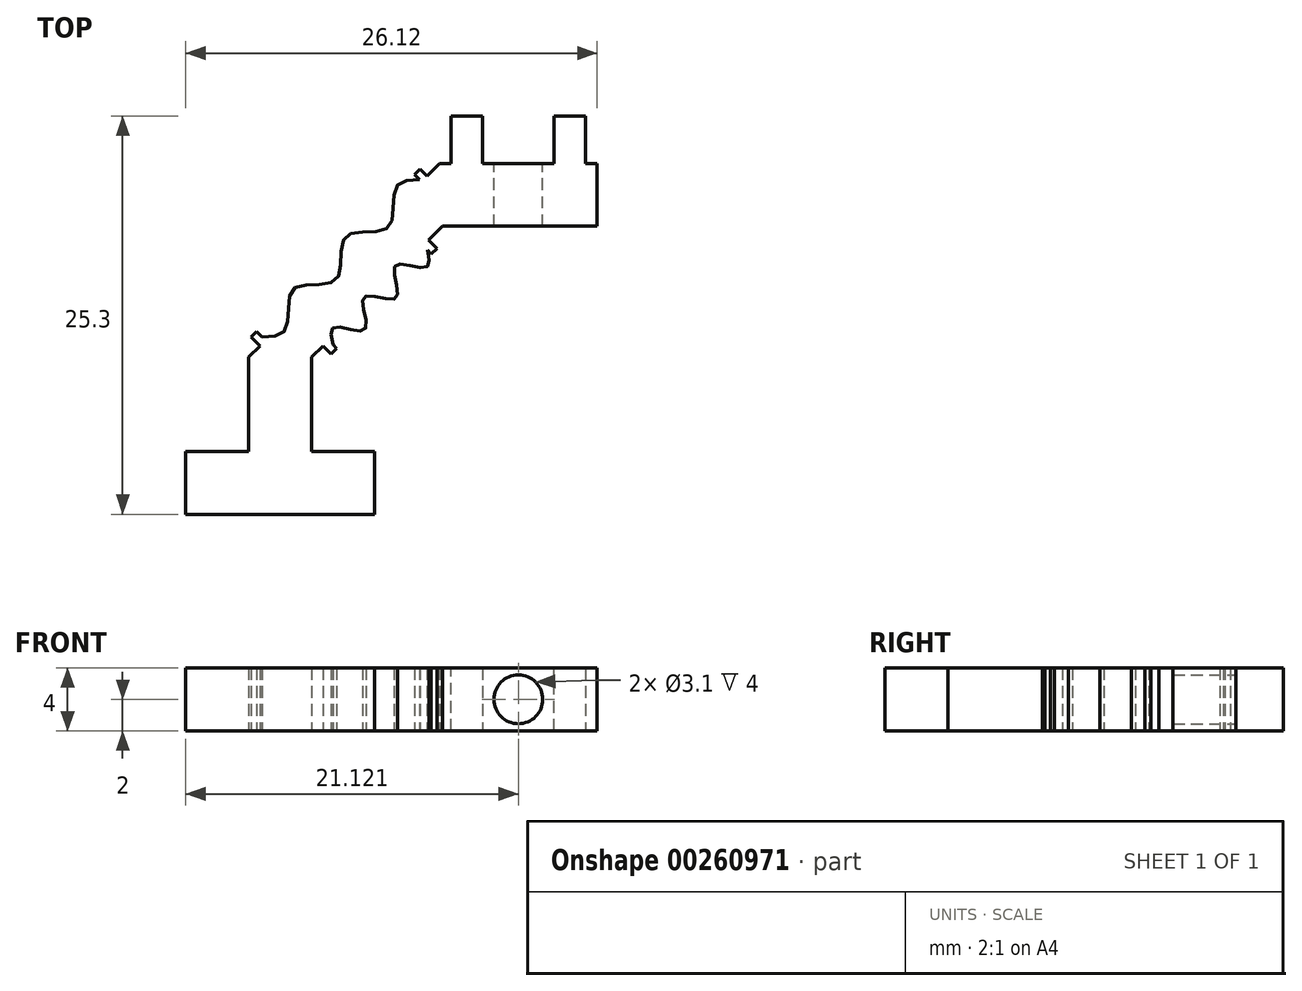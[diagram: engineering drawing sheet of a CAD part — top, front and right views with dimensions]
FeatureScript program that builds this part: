
annotation { "Feature Type Name" : "Feature", "Feature Type Description" : "" }
export const myFeature = defineFeature(function(context is Context, id is Id, definition is map)
    precondition{}
    {
        {
            var Q0;
            Q0=qCreatedBy(makeId("Top.planeOp"),FACE);
            var sketch = newSketch(context, id + "F0", { "sketchPlane" : qUnion([Q0])});
            skLineSegment(sketch, "E0", {"start": v(8, 0) * mm, "end": v(4, 0) * mm});
            skLineSegment(sketch, "E1", {"start": v(4, 4) * mm, "end": v(4, 10) * mm});
            skLineSegment(sketch, "E2", {"start": v(8, 4) * mm, "end": v(12, 4) * mm});
            skLineSegment(sketch, "E3", {"start": v(12, 4) * mm, "end": v(12, 0) * mm});
            skLineSegment(sketch, "E4", {"start": v(12, 0) * mm, "end": v(8, 0) * mm});
            skLineSegment(sketch, "E5", {"start": v(4, 0) * mm, "end": v(0, 0) * mm});
            skLineSegment(sketch, "E6", {"start": v(0, 0) * mm, "end": v(0, 4) * mm});
            skLineSegment(sketch, "E7", {"start": v(0, 4) * mm, "end": v(4, 4) * mm});
            skLineSegment(sketch, "E8", {"start": v(8, 4) * mm, "end": v(8, 10) * mm});
            skLineSegment(sketch, "E9", {"start": v(5.33, 10.8) * mm, "end": v(7, 12.46) * mm, "construction": true});
            skLineSegment(sketch, "E10", {"start": v(7, 12.46) * mm, "end": v(8.66, 14.13) * mm, "construction": true});
            skLineSegment(sketch, "E11", {"start": v(8.66, 14.13) * mm, "end": v(10.33, 15.8) * mm, "construction": true});
            skLineSegment(sketch, "E12", {"start": v(10.33, 15.8) * mm, "end": v(12, 17.46) * mm, "construction": true});
            skLineSegment(sketch, "E13", {"start": v(12, 17.46) * mm, "end": v(13.66, 19.13) * mm, "construction": true});
            skLineSegment(sketch, "E14", {"start": v(13.66, 19.13) * mm, "end": v(15.33, 20.8) * mm, "construction": true});
            skLineSegment(sketch, "E15", {"start": v(6.16, 11.63) * mm, "end": v(6.69, 11.1) * mm, "construction": true});
            skLineSegment(sketch, "E16", {"start": v(7.83, 13.3) * mm, "end": v(7.3, 13.83) * mm, "construction": true});
            skLineSegment(sketch, "E17", {"start": v(9.5, 14.96) * mm, "end": v(10.02, 14.43) * mm, "construction": true});
            skLineSegment(sketch, "E18", {"start": v(11.16, 16.63) * mm, "end": v(10.63, 17.16) * mm, "construction": true});
            skLineSegment(sketch, "E19", {"start": v(12.83, 18.3) * mm, "end": v(13.36, 17.77) * mm, "construction": true});
            skLineSegment(sketch, "E20", {"start": v(14.5, 19.96) * mm, "end": v(13.96, 20.5) * mm, "construction": true});
            skLineSegment(sketch, "E21", {"start": v(8.8, 11.33) * mm, "end": v(9.8, 12.33) * mm, "construction": true});
            skLineSegment(sketch, "E22", {"start": v(9.8, 12.33) * mm, "end": v(10.8, 13.33) * mm, "construction": true});
            skLineSegment(sketch, "E23", {"start": v(10.8, 13.33) * mm, "end": v(11.8, 14.33) * mm, "construction": true});
            skLineSegment(sketch, "E24", {"start": v(11.8, 14.33) * mm, "end": v(12.8, 15.33) * mm, "construction": true});
            skLineSegment(sketch, "E25", {"start": v(12.8, 15.33) * mm, "end": v(13.8, 16.33) * mm, "construction": true});
            skLineSegment(sketch, "E26", {"start": v(13.8, 16.33) * mm, "end": v(14.8, 17.33) * mm, "construction": true});
            skLineSegment(sketch, "E27", {"start": v(9.3, 11.83) * mm, "end": v(8.77, 12.36) * mm, "construction": true});
            skLineSegment(sketch, "E28", {"start": v(10.3, 12.83) * mm, "end": v(10.83, 12.3) * mm});
            skLineSegment(sketch, "E29", {"start": v(11.3, 13.83) * mm, "end": v(10.77, 14.36) * mm, "construction": true});
            skLineSegment(sketch, "E30", {"start": v(12.3, 14.83) * mm, "end": v(12.83, 14.3) * mm, "construction": true});
            skLineSegment(sketch, "E31", {"start": v(13.3, 15.83) * mm, "end": v(12.77, 16.36) * mm, "construction": true});
            skLineSegment(sketch, "E32", {"start": v(14.3, 16.83) * mm, "end": v(14.83, 16.3) * mm, "construction": true});
            skFitSpline(sketch, "E33", {"points": [v(5.27, 10.85) * mm, v(6.64, 11.15) * mm, v(6.94, 12.52) * mm, v(7.24, 13.88) * mm, v(8.6, 14.18) * mm, v(9.97, 14.48) * mm, v(10.27, 15.85) * mm, v(10.58, 17.21) * mm, v(11.94, 17.52) * mm, v(13.3, 17.82) * mm, v(13.6, 19.18) * mm, v(13.9, 20.55) * mm, v(15.27, 20.85) * mm], "startDerivative": vector(19.55, 0.45) * mm, "endDerivative": vector(19.55, 0.45) * mm});
            skLineSegment(sketch, "E34", {"start": v(15.33, 20.8) * mm, "end": v(14.8, 21.33) * mm});
            skFitSpline(sketch, "E35", {"points": [v(8.78, 11.34) * mm, v(8.75, 12.37) * mm, v(9.78, 12.34) * mm, v(10.8, 12.31) * mm, v(10.78, 13.34) * mm, v(10.75, 14.37) * mm, v(11.78, 14.34) * mm, v(12.8, 14.31) * mm, v(12.78, 15.34) * mm, v(12.75, 16.37) * mm, v(13.78, 16.34) * mm, v(14.8, 16.31) * mm, v(14.78, 17.34) * mm], "startDerivative": vector(-3.55, 15.55) * mm, "endDerivative": vector(-3.54, 15.55) * mm});
            skFitSpline(sketch, "E36", {"points": [v(9.34, 10.78) * mm, v(9.31, 11.8) * mm, v(10.34, 11.78) * mm, v(11.37, 11.75) * mm, v(11.34, 12.78) * mm, v(11.31, 13.8) * mm, v(12.34, 13.78) * mm, v(13.37, 13.75) * mm, v(13.34, 14.78) * mm, v(13.31, 15.8) * mm, v(14.34, 15.78) * mm, v(15.37, 15.75) * mm, v(15.34, 16.78) * mm], "startDerivative": vector(-3.55, 15.55) * mm, "endDerivative": vector(-3.54, 15.55) * mm});
            skLineSegment(sketch, "E37", {"start": v(16.3, 18.3) * mm, "end": v(26.12, 18.3) * mm});
            skLineSegment(sketch, "E38", {"start": v(26.12, 18.3) * mm, "end": v(26.12, 22.3) * mm});
            skLineSegment(sketch, "E39", {"start": v(26.12, 22.3) * mm, "end": v(16.12, 22.3) * mm});
            skLineSegment(sketch, "E40", {"start": v(8, 10) * mm, "end": v(8.88, 10.88) * mm});
            skLineSegment(sketch, "E41", {"start": v(14.53, 17.6) * mm, "end": v(14.88, 17.94) * mm});
            skLineSegment(sketch, "E42", {"start": v(15.6, 16.53) * mm, "end": v(15.94, 16.88) * mm});
            skLineSegment(sketch, "E43", {"start": v(15.94, 16.88) * mm, "end": v(14.88, 17.94) * mm});
            skLineSegment(sketch, "E44", {"start": v(15.41, 17.41) * mm, "end": v(16.3, 18.3) * mm});
            skPoint(sketch, "E45.endSnap0", {"position": v(5.46, 10.66) * mm});
            skLineSegment(sketch, "E46", {"start": v(4, 10) * mm, "end": v(4.88, 10.88) * mm});
            skLineSegment(sketch, "E47", {"start": v(15.33, 20.8) * mm, "end": v(15.41, 20.7) * mm});
            skLineSegment(sketch, "E48", {"start": v(14.8, 21.33) * mm, "end": v(14.53, 21.6) * mm});
            skLineSegment(sketch, "E49", {"start": v(14.53, 21.6) * mm, "end": v(14.88, 21.94) * mm});
            skLineSegment(sketch, "E50", {"start": v(15.41, 20.7) * mm, "end": v(15.77, 21.06) * mm});
            skLineSegment(sketch, "E51", {"start": v(14.88, 21.94) * mm, "end": v(15.77, 21.06) * mm});
            skLineSegment(sketch, "E52", {"start": v(15.33, 21.5) * mm, "end": v(16.12, 22.3) * mm});
            skLineSegment(sketch, "E53", {"start": v(14.53, 17.6) * mm, "end": v(15.6, 16.53) * mm});
            skLineSegment(sketch, "E54", {"start": v(4.5, 11.63) * mm, "end": v(5.63, 10.5) * mm});
            skLineSegment(sketch, "E55", {"start": v(4.88, 10.88) * mm, "end": v(5.06, 11.06) * mm});
            skLineSegment(sketch, "E56", {"start": v(4.8, 11.33) * mm, "end": v(5.06, 11.06) * mm});
            skLineSegment(sketch, "E57", {"start": v(5.06, 11.06) * mm, "end": v(4.85, 11.27) * mm});
            skFitSpline(sketch, "E58", {"points": [v(4.85, 11.27) * mm, v(6.21, 11.58) * mm, v(6.52, 12.94) * mm, v(6.82, 14.3) * mm, v(8.18, 14.6) * mm, v(9.55, 14.9) * mm, v(9.85, 16.27) * mm, v(10.15, 17.64) * mm, v(11.52, 17.94) * mm, v(12.88, 18.24) * mm, v(13.18, 19.6) * mm, v(13.48, 20.97) * mm, v(14.85, 21.27) * mm], "startDerivative": vector(19.55, 0.45) * mm, "endDerivative": vector(19.55, 0.45) * mm});
            skLineSegment(sketch, "E59", {"start": v(5.06, 11.06) * mm, "end": v(5.27, 10.85) * mm});
            skLineSegment(sketch, "E60", {"start": v(9.06, 11.06) * mm, "end": v(8.78, 11.34) * mm});
            skLineSegment(sketch, "E61", {"start": v(9.06, 11.06) * mm, "end": v(9.34, 10.78) * mm});
            skLineSegment(sketch, "E62", {"start": v(8.53, 11.6) * mm, "end": v(9.6, 10.53) * mm});
            skLineSegment(sketch, "E63", {"start": v(8.53, 11.6) * mm, "end": v(9.06, 11.06) * mm});
            skLineSegment(sketch, "E64", {"start": v(4.5, 11.63) * mm, "end": v(4.14, 11.27) * mm});
            skLineSegment(sketch, "E65", {"start": v(5.63, 10.5) * mm, "end": v(5.27, 10.14) * mm});
            skLineSegment(sketch, "E66", {"start": v(4.14, 11.27) * mm, "end": v(5.27, 10.14) * mm});
            skLineSegment(sketch, "E67", {"start": v(9.6, 10.53) * mm, "end": v(9.24, 10.18) * mm});
            skLineSegment(sketch, "E68", {"start": v(8.53, 11.6) * mm, "end": v(8.18, 11.24) * mm});
            skLineSegment(sketch, "E69", {"start": v(8.18, 11.24) * mm, "end": v(9.24, 10.18) * mm});
            skSolve(sketch);
        }
        {
            var Q0;
            Q0 = qSketchRegion(id + "F0", true);
            extrude(context, id + "F1", {"entities" : qUnion([Q0]), "depth" : 4 * mm});
        }
        {
            var Q0;
            Q0=makeQuery(id+"F1.opExtrude","SWEPT_FACE",FACE,{"disambiguationData":[OSD([sQuery(id+"F0.wireOp",EDGE,"E39")])]});
            var sketch = newSketch(context, id + "F2", { "sketchPlane" : qUnion([Q0])});
            skLineSegment(sketch, "E70", {"start": v(-26.12, 4) * mm, "end": v(-25.4, 4) * mm});
            skLineSegment(sketch, "E71", {"start": v(-25.4, 4) * mm, "end": v(-25.4, 0) * mm});
            skLineSegment(sketch, "E72", {"start": v(-25.4, 0) * mm, "end": v(-23.4, 0) * mm});
            skLineSegment(sketch, "E73", {"start": v(-23.4, 0) * mm, "end": v(-23.4, 4) * mm});
            skLineSegment(sketch, "E74", {"start": v(-25.4, 4) * mm, "end": v(-23.4, 4) * mm});
            skLineSegment(sketch, "E75", {"start": v(-18.85, 4) * mm, "end": v(-18.85, 0) * mm});
            skLineSegment(sketch, "E76", {"start": v(-18.85, 0) * mm, "end": v(-16.85, 0) * mm});
            skLineSegment(sketch, "E77", {"start": v(-16.85, 0) * mm, "end": v(-16.85, 4) * mm});
            skLineSegment(sketch, "E78", {"start": v(-16.85, 4) * mm, "end": v(-18.85, 4) * mm});
            skSolve(sketch);
        }
        {
            var Q0;
            Q0 = qSketchRegion(id + "F2", true);
            extrude(context, id + "F3", {"entities" : qUnion([Q0]), "operationType" : NewBodyOperationType.ADD, "depth" : 3 * mm});
        }
        {
            var Q0;
            {var subQ16=sQuery(id+"F0.wireOp",EDGE,"E39");Q0=makeQuery(id+"F3.boolean.opBoolean","SPLIT",FACE,{"disambiguationData":[TD([makeQuery(id+"F3.opExtrude","SWEPT_FACE",FACE,{"disambiguationData":[OSD([sQuery(id+"F2.wireOp",EDGE,"E73")])]})])],"derivedFrom":makeQuery(id+"F1.opExtrude","SWEPT_FACE",FACE,{"disambiguationData":[OSD([subQ16])]})});}
            var sketch = newSketch(context, id + "F4", { "sketchPlane" : qUnion([Q0])});
            skCircle(sketch, "E79", {"center": v(-21.12, 2) * mm, "radius": 1.55 * mm});
            skSolve(sketch);
        }
        {
            var Q0;
            Q0 = qSketchRegion(id + "F4", true);
            extrude(context, id + "F5", {"entities" : qUnion([Q0]), "operationType" : NewBodyOperationType.REMOVE, "oppositeDirection" : true, "depth" : 4 * mm});
        }
        {
            var Q0;
            Q0=makeQuery(id+"F1.opExtrude","SWEPT_BODY",BODY,{"disambiguationData":[OSD([sQuery(id+"F0.wireOp",EDGE,"E0"),sQuery(id+"F0.wireOp",EDGE,"E1"),sQuery(id+"F0.wireOp",EDGE,"E2"),sQuery(id+"F0.wireOp",EDGE,"E3"),sQuery(id+"F0.wireOp",EDGE,"E4"),sQuery(id+"F0.wireOp",EDGE,"E5"),sQuery(id+"F0.wireOp",EDGE,"E6"),sQuery(id+"F0.wireOp",EDGE,"E7"),sQuery(id+"F0.wireOp",EDGE,"E8"),sQuery(id+"F0.wireOp",EDGE,"E34"),sQuery(id+"F0.wireOp",EDGE,"E36"),sQuery(id+"F0.wireOp",EDGE,"E37"),sQuery(id+"F0.wireOp",EDGE,"E38"),sQuery(id+"F0.wireOp",EDGE,"E39"),sQuery(id+"F0.wireOp",EDGE,"E40"),sQuery(id+"F0.wireOp",EDGE,"E42"),sQuery(id+"F0.wireOp",EDGE,"E43"),sQuery(id+"F0.wireOp",EDGE,"E44"),sQuery(id+"F0.wireOp",EDGE,"E46"),sQuery(id+"F0.wireOp",EDGE,"E48"),sQuery(id+"F0.wireOp",EDGE,"E49"),sQuery(id+"F0.wireOp",EDGE,"E51"),sQuery(id+"F0.wireOp",EDGE,"E52"),sQuery(id+"F0.wireOp",EDGE,"E53"),sQuery(id+"F0.wireOp",EDGE,"E54"),sQuery(id+"F0.wireOp",EDGE,"E56"),sQuery(id+"F0.wireOp",EDGE,"E58"),sQuery(id+"F0.wireOp",EDGE,"E62"),sQuery(id+"F0.wireOp",EDGE,"E64"),sQuery(id+"F0.wireOp",EDGE,"E66"),sQuery(id+"F0.wireOp",EDGE,"E67"),sQuery(id+"F0.wireOp",EDGE,"E69")])]});
            transform(context, id + "F6", {"entities" : qUnion([Q0]), "transformType" : TransformType.TRANSLATION_3D, "dx" : 0 * mm, "dy" : 0 * mm, "dz" : 0 * mm, "makeCopy" : true});
        }
    });
